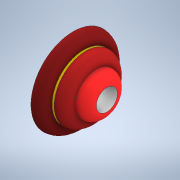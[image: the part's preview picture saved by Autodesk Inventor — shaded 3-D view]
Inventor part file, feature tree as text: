
AUTODESK INVENTOR PART (.ipt)
format: ipt  version: 2021 (Build 250183000, 183)  size: 173,568 bytes
history: native  units: mm
features: revolve x1, fillet x1, sketch x1
ambient origin geometry x8: Origin, YZ Plane, XZ Plane, XY Plane, X Axis, Y Axis, Z Axis, Center Point
bodies: Solid1 (feature_tree)
feature tree (3):
  revolve  "Revolution1"  [1 undecoded]
  fillet  "Fillet1"  Radius=15.0mm
  sketch  "Sketch1"  dims[d0=20.0mm d1=5.0mm d2=15.0mm d3=6.0mm d4=10.0mm d5=5.0mm d6=5.0mm d7=5.0mm d8=90.0deg d9=5.0mm]
note: 1 required parameter value undecoded (feature->parameter linkage not recoverable at this tier; creation-order binding heuristic only, values carry confidence <= 0.55)
